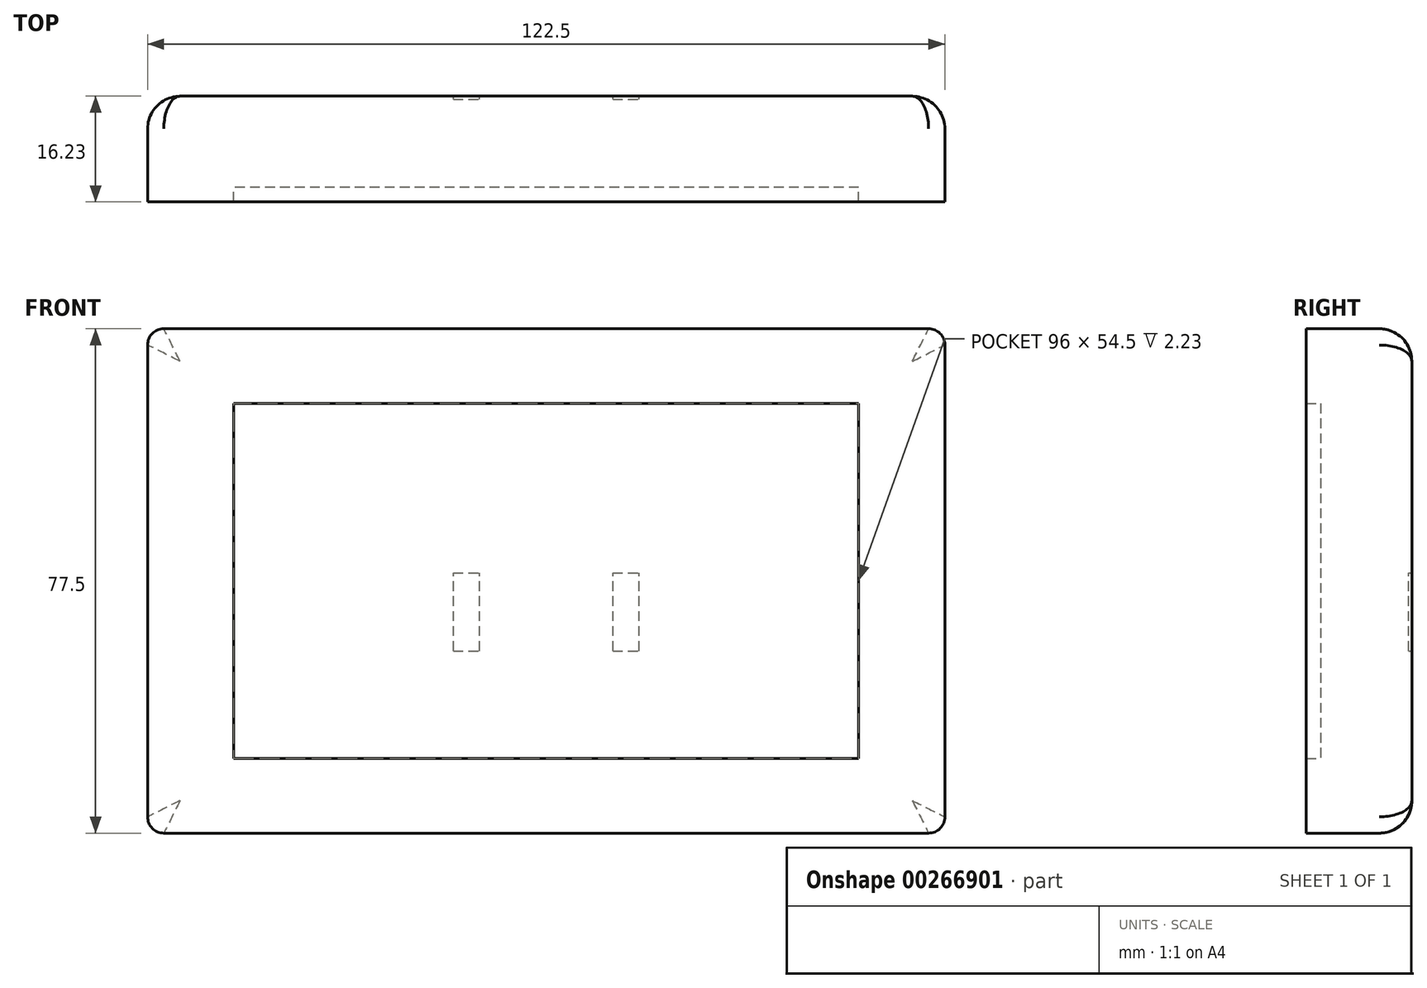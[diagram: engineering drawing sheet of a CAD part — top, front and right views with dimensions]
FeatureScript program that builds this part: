
annotation { "Feature Type Name" : "Feature", "Feature Type Description" : "" }
export const myFeature = defineFeature(function(context is Context, id is Id, definition is map)
    precondition{}
    {
        {
            var Q0;
            Q0=qCreatedBy(makeId("Front.planeOp"),FACE);
            var sketch = newSketch(context, id + "F0", { "sketchPlane" : qUnion([Q0])});
            skLineSegment(sketch, "E0.bottom", {"start": v(61.25, 38.75) * mm, "end": v(-61.25, 38.75) * mm});
            skLineSegment(sketch, "E0.top", {"start": v(61.25, -38.75) * mm, "end": v(-61.25, -38.75) * mm});
            skLineSegment(sketch, "E0.left", {"start": v(61.25, 38.75) * mm, "end": v(61.25, -38.75) * mm});
            skLineSegment(sketch, "E0.right", {"start": v(-61.25, 38.75) * mm, "end": v(-61.25, -38.75) * mm});
            skPoint(sketch, "E0.middle", {"position": v(0, 0) * mm});
            skLineSegment(sketch, "E1.bottom", {"start": v(48, 27.25) * mm, "end": v(-48, 27.25) * mm});
            skLineSegment(sketch, "E1.top", {"start": v(48, -27.25) * mm, "end": v(-48, -27.25) * mm});
            skLineSegment(sketch, "E1.left", {"start": v(48, 27.25) * mm, "end": v(48, -27.25) * mm});
            skLineSegment(sketch, "E1.right", {"start": v(-48, 27.25) * mm, "end": v(-48, -27.25) * mm});
            skLineSegment(sketch, "E2.bottom", {"start": v(10.25, -10.75) * mm, "end": v(14.25, -10.75) * mm});
            skLineSegment(sketch, "E2.top", {"start": v(10.25, 1.25) * mm, "end": v(14.25, 1.25) * mm});
            skLineSegment(sketch, "E2.left", {"start": v(10.25, -10.75) * mm, "end": v(10.25, 1.25) * mm});
            skLineSegment(sketch, "E2.right", {"start": v(14.25, -10.75) * mm, "end": v(14.25, 1.25) * mm});
            skPoint(sketch, "E2.middle", {"position": v(12.25, -4.75) * mm});
            skLineSegment(sketch, "E3.bottom", {"start": v(-14.25, -10.75) * mm, "end": v(-10.25, -10.75) * mm});
            skLineSegment(sketch, "E3.top", {"start": v(-14.25, 1.25) * mm, "end": v(-10.25, 1.25) * mm});
            skLineSegment(sketch, "E3.left", {"start": v(-14.25, -10.75) * mm, "end": v(-14.25, 1.25) * mm});
            skLineSegment(sketch, "E3.right", {"start": v(-10.25, -10.75) * mm, "end": v(-10.25, 1.25) * mm});
            skPoint(sketch, "E3.middle", {"position": v(-12.25, -4.75) * mm});
            skSolve(sketch);
        }
        {
            var Q0;
            Q0=makeQuery(id+"F0.imprint","IMPRINT",FACE,{"disambiguationData":[TD([[makeQuery(id+"F0.imprint","IMPRINT",EDGE,{"derivedFrom":sQuery(id+"F0.wireOp",EDGE,"E0.bottom")}),1.0]])]});
            extrude(context, id + "F1", {"entities" : qUnion([Q0]), "depth" : 16.23 * mm});
        }
        {
            var Q0;
            Q0=makeQuery(id+"F0.imprint","IMPRINT",FACE,{"disambiguationData":[TD([[makeQuery(id+"F0.imprint","IMPRINT",EDGE,{"derivedFrom":sQuery(id+"F0.wireOp",EDGE,"E1.bottom")}),1.0]])]});
            var Q1;
            Q1=makeQuery(id+"F0.imprint","IMPRINT",FACE,{"disambiguationData":[TD([[makeQuery(id+"F0.imprint","IMPRINT",EDGE,{"derivedFrom":sQuery(id+"F0.wireOp",EDGE,"E3.bottom")}),1.0]])]});
            var Q2;
            Q2=makeQuery(id+"F0.imprint","IMPRINT",FACE,{"disambiguationData":[TD([[makeQuery(id+"F0.imprint","IMPRINT",EDGE,{"derivedFrom":sQuery(id+"F0.wireOp",EDGE,"E2.bottom")}),1.0]])]});
            extrude(context, id + "F2", {"entities" : qUnion([Q0, Q1, Q2]), "operationType" : NewBodyOperationType.ADD, "depth" : 14 * mm});
        }
        {
            var Q0;
            Q0=makeQuery(id+"F1.opExtrude","SWEPT_EDGE",EDGE,{"disambiguationData":[OSD([sQuery(id+"F0.wireOp",EDGE,"E0.bottom"),sQuery(id+"F0.wireOp",EDGE,"E0.right")])]});
            var Q1;
            Q1=makeQuery(id+"F1.opExtrude","SWEPT_EDGE",EDGE,{"disambiguationData":[OSD([sQuery(id+"F0.wireOp",EDGE,"E0.bottom"),sQuery(id+"F0.wireOp",EDGE,"E0.left")])]});
            var Q2;
            Q2=makeQuery(id+"F1.opExtrude","SWEPT_EDGE",EDGE,{"disambiguationData":[OSD([sQuery(id+"F0.wireOp",EDGE,"E0.top"),sQuery(id+"F0.wireOp",EDGE,"E0.left")])]});
            var Q3;
            Q3=makeQuery(id+"F1.opExtrude","SWEPT_EDGE",EDGE,{"disambiguationData":[OSD([sQuery(id+"F0.wireOp",EDGE,"E0.top"),sQuery(id+"F0.wireOp",EDGE,"E0.right")])]});
            fillet(context, id + "F3", {"entities" : qUnion([Q0, Q1, Q2, Q3]), "radius" : 2.5 * mm, "tangentPropagation" : true, "allowEdgeOverflow" : false});
        }
        {
            var Q0;
            Q0=makeQuery(id+"F1.opExtrude","CAP_EDGE",EDGE,{"disambiguationData":[OSD([sQuery(id+"F0.wireOp",EDGE,"E0.bottom")])],"isStart":true});
            fillet(context, id + "F4", {"entities" : qUnion([Q0]), "radius" : 5 * mm, "tangentPropagation" : true, "allowEdgeOverflow" : false});
        }
        {
            var Q0;
            Q0=makeQuery(id+"F0.imprint","IMPRINT",FACE,{"disambiguationData":[TD([[makeQuery(id+"F0.imprint","IMPRINT",EDGE,{"derivedFrom":sQuery(id+"F0.wireOp",EDGE,"E2.bottom")}),1.0]])]});
            var Q1;
            Q1=makeQuery(id+"F0.imprint","IMPRINT",FACE,{"disambiguationData":[TD([[makeQuery(id+"F0.imprint","IMPRINT",EDGE,{"derivedFrom":sQuery(id+"F0.wireOp",EDGE,"E3.bottom")}),1.0]])]});
            extrude(context, id + "F5", {"entities" : qUnion([Q0, Q1]), "operationType" : NewBodyOperationType.REMOVE, "depth" : .5 * mm});
        }
    });
